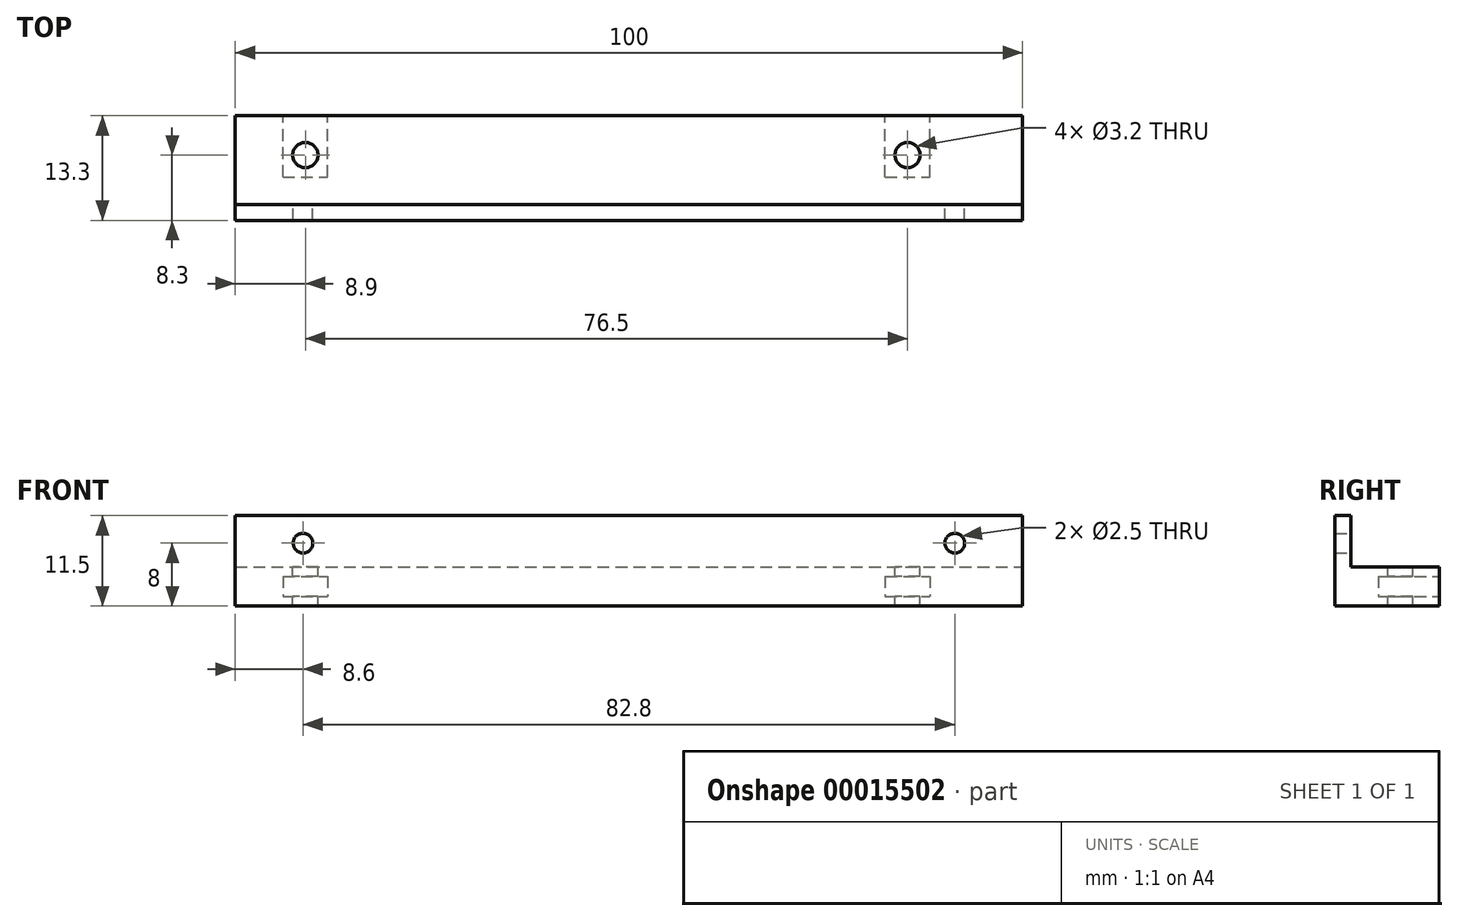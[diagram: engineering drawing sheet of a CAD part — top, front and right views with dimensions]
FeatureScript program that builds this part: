
annotation { "Feature Type Name" : "Feature", "Feature Type Description" : "" }
export const myFeature = defineFeature(function(context is Context, id is Id, definition is map)
    precondition{}
    {
        {
            var Q0;
            Q0=qCreatedBy(makeId("Top.planeOp"),FACE);
            var sketch = newSketch(context, id + "F0", { "sketchPlane" : qUnion([Q0])});
            skLineSegment(sketch, "E0.rect.bottom", {"start": v(50, 0) * mm, "end": v(-50, 0) * mm});
            skLineSegment(sketch, "E0.rect.top", {"start": v(50, -2) * mm, "end": v(-50, -2) * mm});
            skLineSegment(sketch, "E0.rect.left", {"start": v(50, 0) * mm, "end": v(50, -2) * mm});
            skLineSegment(sketch, "E0.rect.right", {"start": v(-50, 0) * mm, "end": v(-50, -2) * mm});
            skPoint(sketch, "E0.rect.middle", {"position": v(0, 0) * mm});
            skSolve(sketch);
        }
        {
            var Q0;
            Q0 = qSketchRegion(id + "F0", true);
            extrude(context, id + "F1", {"entities" : qUnion([Q0]), "depth" : 6.5 * mm});
        }
        {
            var Q0;
            Q0=qCreatedBy(makeId("Front.planeOp"),FACE);
            var sketch = newSketch(context, id + "F2", { "sketchPlane" : qUnion([Q0])});
            skPoint(sketch, "E1", {"position": v(-41.4, 3) * mm});
            skPoint(sketch, "E2", {"position": v(41.4, 3) * mm});
            skLineSegment(sketch, "E3", {"start": v(-41.4, 3) * mm, "end": v(41.4, 3) * mm, "construction": true});
            skLineSegment(sketch, "E4", {"start": v(0, 0) * mm, "end": v(0, 3) * mm, "construction": true});
            skSolve(sketch);
        }
        {
            var Q0;
            Q0=sQuery(id+"F2.wireOp",VERTEX,"E2");
            var Q1;
            Q1=sQuery(id+"F2.wireOp",VERTEX,"E1");
            var Q2;
            Q2=makeQuery(id+"F1.opExtrude","SWEPT_BODY",BODY,{"disambiguationData":[OSD([sQuery(id+"F0.wireOp",EDGE,"E0.rect.bottom"),sQuery(id+"F0.wireOp",EDGE,"E0.rect.top"),sQuery(id+"F0.wireOp",EDGE,"E0.rect.left"),sQuery(id+"F0.wireOp",EDGE,"E0.rect.right")])]});
            hole(context, id + "F3", {"style" : HoleStyle.SIMPLE, "holeDiameter" : 2.5 * mm, "endStyle" : HoleEndStyle.THROUGH, "oppositeDirection" : true, "locations" : qUnion([Q0, Q1]), "scope" : qUnion([Q2])});
        }
        {
            var Q0;
            Q0=qCreatedBy(makeId("Top.planeOp"),FACE);
            var sketch = newSketch(context, id + "F4", { "sketchPlane" : qUnion([Q0])});
            skLineSegment(sketch, "E5.bottom", {"start": v(-50, -2) * mm, "end": v(50, -2) * mm});
            skLineSegment(sketch, "E5.top", {"start": v(-50, 11.3) * mm, "end": v(50, 11.3) * mm});
            skLineSegment(sketch, "E5.left", {"start": v(-50, -2) * mm, "end": v(-50, 11.3) * mm});
            skLineSegment(sketch, "E5.right", {"start": v(50, -2) * mm, "end": v(50, 11.3) * mm});
            skSolve(sketch);
        }
        {
            var Q0;
            Q0 = qSketchRegion(id + "F4", true);
            extrude(context, id + "F5", {"entities" : qUnion([Q0]), "operationType" : NewBodyOperationType.ADD, "oppositeDirection" : true, "depth" : 5 * mm});
        }
        {
            var Q0;
            Q0=qCreatedBy(makeId("Top.planeOp"),FACE);
            var sketch = newSketch(context, id + "F6", { "sketchPlane" : qUnion([Q0])});
            skPoint(sketch, "E6", {"position": v(-41.1, 6.3) * mm});
            skLineSegment(sketch, "E7", {"start": v(-41.1, 6.3) * mm, "end": v(35.4, 6.3) * mm, "construction": true});
            skPoint(sketch, "E8", {"position": v(35.4, 6.3) * mm});
            skSolve(sketch);
        }
        {
            var Q0;
            Q0=sQuery(id+"F6.wireOp",VERTEX,"E6");
            var Q1;
            Q1=sQuery(id+"F6.wireOp",VERTEX,"E8");
            var Q2;
            Q2=makeQuery(id+"F1.opExtrude","SWEPT_BODY",BODY,{"disambiguationData":[OSD([sQuery(id+"F0.wireOp",EDGE,"E0.rect.bottom"),sQuery(id+"F0.wireOp",EDGE,"E0.rect.top"),sQuery(id+"F0.wireOp",EDGE,"E0.rect.left"),sQuery(id+"F0.wireOp",EDGE,"E0.rect.right")])]});
            hole(context, id + "F7", {"style" : HoleStyle.SIMPLE, "holeDiameter" : 3.2 * mm, "endStyle" : HoleEndStyle.THROUGH, "locations" : qUnion([Q0, Q1]), "scope" : qUnion([Q2])});
        }
        {
            var Q0;
            Q0=makeQuery(id+"F5.opExtrude","SWEPT_FACE",FACE,{"disambiguationData":[OSD([sQuery(id+"F4.wireOp",EDGE,"E5.top")])]});
            var sketch = newSketch(context, id + "F8", { "sketchPlane" : qUnion([Q0])});
            skLineSegment(sketch, "E9.rect.bottom", {"start": v(-32.55, -1.2) * mm, "end": v(-38.25, -1.2) * mm});
            skLineSegment(sketch, "E9.rect.top", {"start": v(-32.55, -3.8) * mm, "end": v(-38.25, -3.8) * mm});
            skLineSegment(sketch, "E9.rect.left", {"start": v(-32.55, -1.2) * mm, "end": v(-32.55, -3.8) * mm});
            skLineSegment(sketch, "E9.rect.right", {"start": v(-38.25, -1.2) * mm, "end": v(-38.25, -3.8) * mm});
            skPoint(sketch, "E9.rect.middle", {"position": v(-35.4, -2.5) * mm});
            skLineSegment(sketch, "E10", {"start": v(-35.4, -2.5) * mm, "end": v(-35.4, 0) * mm, "construction": true});
            skLineSegment(sketch, "E11", {"start": v(41.1, 0) * mm, "end": v(41.1, -2.5) * mm, "construction": true});
            skLineSegment(sketch, "E12.rect.bottom", {"start": v(43.95, -1.2) * mm, "end": v(38.25, -1.2) * mm});
            skLineSegment(sketch, "E12.rect.top", {"start": v(43.95, -3.8) * mm, "end": v(38.25, -3.8) * mm});
            skLineSegment(sketch, "E12.rect.left", {"start": v(43.95, -1.2) * mm, "end": v(43.95, -3.8) * mm});
            skLineSegment(sketch, "E12.rect.right", {"start": v(38.25, -1.2) * mm, "end": v(38.25, -3.8) * mm});
            skPoint(sketch, "E12.rect.middle", {"position": v(41.1, -2.5) * mm});
            skSolve(sketch);
        }
        {
            var Q0;
            Q0 = qSketchRegion(id + "F8", true);
            extrude(context, id + "F9", {"entities" : qUnion([Q0]), "operationType" : NewBodyOperationType.REMOVE, "oppositeDirection" : true, "depth" : (5 + 2.8) * mm});
        }
    });
